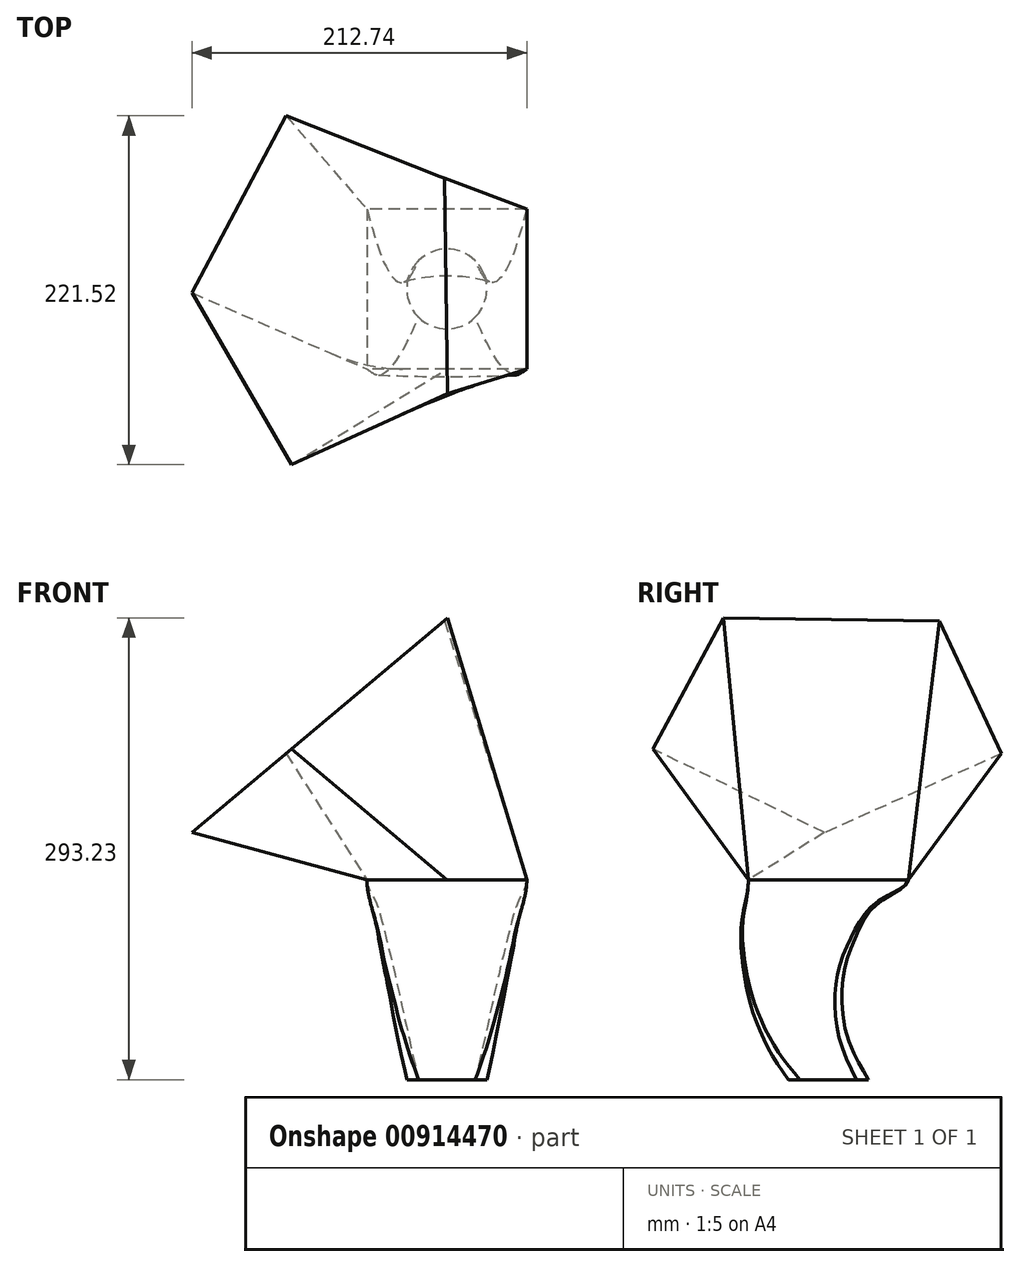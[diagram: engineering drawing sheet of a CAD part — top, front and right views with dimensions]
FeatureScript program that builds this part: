
annotation { "Feature Type Name" : "Feature", "Feature Type Description" : "" }
export const myFeature = defineFeature(function(context is Context, id is Id, definition is map)
    precondition{}
    {
        {
            var Q0;
            Q0=qCreatedBy(makeId("Top.planeOp"),FACE);
            var sketch = newSketch(context, id + "F0", { "sketchPlane" : qUnion([Q0])});
            skCircle(sketch, "E0", {"center": v(0, 0) * mm, "radius": 25.4 * mm});
            skSolve(sketch);
        }
        {
            var Q0;
            Q0=qCreatedBy(makeId("Top.planeOp"),FACE);
            cPlane(context, id + "F1", {"entities" : qUnion([Q0]), "cplaneType" : CPlaneType.OFFSET, "offset" : 127 * mm, "width" : 152.4 * mm, "height" : 152.4 * mm});
        }
        {
            var Q0;
            Q0=qCreatedBy(id+"F1.planeOp",FACE);
            var sketch = newSketch(context, id + "F2", { "sketchPlane" : qUnion([Q0])});
            skLineSegment(sketch, "E1.bottom", {"start": v(50.8, 50.8) * mm, "end": v(-50.8, 50.8) * mm});
            skLineSegment(sketch, "E1.top", {"start": v(50.8, -50.8) * mm, "end": v(-50.8, -50.8) * mm});
            skLineSegment(sketch, "E1.left", {"start": v(50.8, 50.8) * mm, "end": v(50.8, -50.8) * mm});
            skLineSegment(sketch, "E1.right", {"start": v(-50.8, 50.8) * mm, "end": v(-50.8, -50.8) * mm});
            skPoint(sketch, "E1.middle", {"position": v(0, 0) * mm});
            skSolve(sketch);
        }
        {
            var Q0;
            Q0=qCreatedBy(makeId("Right.planeOp"),FACE);
            var sketch = newSketch(context, id + "F3", { "sketchPlane" : qUnion([Q0])});
            skArc(sketch, "E2", {"start": v(0, 127) * mm, "mid": v(-21.15, 62.55) * mm, "end": v(0, -1.9) * mm});
            skSolve(sketch);
        }
        {
            var Q0;
            Q0=sQuery(id+"F3.wireOp",EDGE,"E2");
            var Q1;
            Q1=makeQuery(id+"F2.imprint","IMPRINT",FACE,{"disambiguationData":[TD([[makeQuery(id+"F2.imprint","IMPRINT",EDGE,{"derivedFrom":sQuery(id+"F2.wireOp",EDGE,"E1.bottom")}),1.0]])]});
            var Q2;
            Q2=makeQuery(id+"F0.imprint","IMPRINT",FACE,{"disambiguationData":[TD([[makeQuery(id+"F0.imprint","IMPRINT",EDGE,{"derivedFrom":sQuery(id+"F0.wireOp",EDGE,"E0")}),1.0]])]});
            loft(context, id + "F4", {"addSections" : true, "spine" : qUnion([Q0]), "sectionCount" : 5, "startCondition" : LoftEndDerivativeType.NORMAL_TO_PROFILE, "startMagnitude" : 1, "sheetProfilesArray" : [{ "sheetProfileEntities" : qUnion([Q1]) }, { "sheetProfileEntities" : qUnion([Q2]) }]});
        }
        {
            var Q0;
            Q0=qCreatedBy(id+"F1.planeOp",FACE);
            var sketch = newSketch(context, id + "F5", { "sketchPlane" : qUnion([Q0])});
            skLineSegment(sketch, "E3", {"start": v(0, 62.72) * mm, "end": v(0, -36.34) * mm});
            skSolve(sketch);
        }
        {
            var Q0;
            Q0=sQuery(id+"F5.wireOp",EDGE,"E3");
            cPlane(context, id + "F6", {"entities" : qUnion([Q0]), "cplaneType" : CPlaneType.LINE_ANGLE, "offset" : 25.4 * mm, "angle" : 40 * degree, "width" : 152.4 * mm, "height" : 152.4 * mm});
        }
        {
            var Q0;
            Q0=qCreatedBy(id+"F6.planeOp",FACE);
            cPlane(context, id + "F7", {"entities" : qUnion([Q0]), "cplaneType" : CPlaneType.OFFSET, "offset" : 127 * mm, "oppositeDirection" : true, "width" : 152.4 * mm, "height" : 152.4 * mm});
        }
        {
            var Q0;
            Q0=qCreatedBy(id+"F7.planeOp",FACE);
            var sketch = newSketch(context, id + "F8", { "sketchPlane" : qUnion([Q0])});
            skCircle(sketch, "E4.cCircle", {"center": v(93.26, 0) * mm, "radius": 94.24 * mm, "construction": true});
            skLineSegment(sketch, "E4.0", {"start": v(54.99, -110.02) * mm, "end": v(-23.2, 2.4) * mm});
            skLineSegment(sketch, "E4.1", {"start": v(-23.2, 2.4) * mm, "end": v(59.56, 111.5) * mm});
            skLineSegment(sketch, "E4.2", {"start": v(59.56, 111.5) * mm, "end": v(188.9, 66.5) * mm});
            skLineSegment(sketch, "E4.3", {"start": v(188.9, 66.5) * mm, "end": v(186.07, -70.4) * mm});
            skLineSegment(sketch, "E4.4", {"start": v(186.07, -70.4) * mm, "end": v(54.99, -110.02) * mm});
            skPoint(sketch, "E4.0.midPoint", {"position": v(15.9, -53.8) * mm});
            skSolve(sketch);
        }
        {
            var Q1;
            Q1=makeQuery(id+"F8.imprint","IMPRINT",FACE,{"disambiguationData":[TD([[makeQuery(id+"F8.imprint","IMPRINT",EDGE,{"derivedFrom":sQuery(id+"F8.wireOp",EDGE,"E4.0")}),-1.0]])]});
            var Q2;
            Q2=makeQuery(id+"F4.opLoft","CAP_FACE",FACE,{"disambiguationData":[OSD([makeQuery(id+"F2.imprint","IMPRINT",FACE,{"disambiguationData":[TD([[makeQuery(id+"F2.imprint","IMPRINT",EDGE,{"derivedFrom":sQuery(id+"F2.wireOp",EDGE,"E1.bottom")}),1.0]])]})])],"isStart":true});
            loft(context, id + "F9", {"operationType" : NewBodyOperationType.ADD, "sheetProfilesArray" : [{ "sheetProfileEntities" : qUnion([Q1]) }, { "sheetProfileEntities" : qUnion([Q2]) }]});
        }
    });
